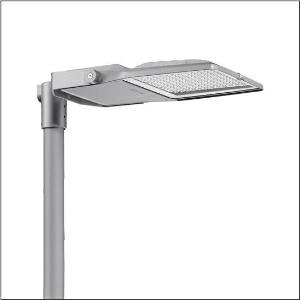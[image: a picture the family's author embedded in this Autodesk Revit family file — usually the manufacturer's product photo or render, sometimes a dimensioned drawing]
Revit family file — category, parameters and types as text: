
# Revit family: floodlight_fl_21_iq_midi___pl61_5xa7781e4c3a_96c8
name_source: partatom
category: Lighting Fixtures
units: mm (PartAtom-declared; Revit-internal decimal feet)

## family parameters
Cut with Voids When Loaded = No
Host = Face
Light Source = No
Part Type = Normal
Room Calculation Point = No
Round Connector Dimension = Use Diameter
Shared = No

## types (1)
- --- (1 x LED, 27490 lm, 208.1 W, 4000K)
    Apparent Load = 208 VA
    CIE Flux Codes = 33 65 98 100 100
    Color Rendering = 70
    Color Temperature = 4000K
    Default Elevation = 1800 mm
    Description = Floodlight FL 21 iQ midi, floodlight, primary light control with lens, of PMMA, primary optical cover: protective disc, of toughened safety glass, transparent, light distribution: PL61, light emission: direct distribution, installation type: surface-mounted, LED, High Power LED, rated luminous flux: 27.490lm, luminous efficacy: 132lm/W, light colour: 740, colour temperature: 4000K, control gear: ECG iQ, control: optimised constant luminous flux control (CLO 2.0), Desk-Remote (wireless, voltage-free reading and setting of iQ features in the workshop via application-optimized NFC function/RFID function), Light-Fading, Smart-Wire, Night-Set, Lumen-Switch, Temp-Guard, Auto-Match, with terminal, 6-pole, mains connection: 220..240V, AC, 50/60Hz, start of lifetime: 208W, end of service life: 227W, reduction: 90W, luminaire housing, of diecast aluminium, powder-coated, Siteco® metallic grey (DB 702S), corrosivity category C5 mid according to DIN EN ISO 12944, sealing non-destructively replaceable, please order mast flange separately, mast bracket, of steel, galvanised, powder-coated, Siteco® metallic grey (DB 702S), protection rating (complete): IP66, insulation class (complete): insulation class II (safety insulation), certification: CE, protection symbol: D, impact resistance: IK08, permissible operating ambient temperature: -40..+40°C, permissible operating ambient temperature for outdoor applications: -40..+50°C, standard: DIN EN 12944, LABS conformity tested according to VDMA 24364:2018-05, packaging unit: 1 piece

Light Distribution: PL61
    Height = 76 mm
    Lamp = 1 x LED
    Lamp Light Flux = 27490 lm
    Lamp Power = 208.1 W
    Lamp count = 1
    Length = 657 mm
    Luminous efficacy = 132 lm/W
    Manufacturer = Siteco
    ModVariant = No
    Model = 5XA7781E4C3A
    Number of Poles = 1
    OnlyDefault = Yes
    Power Factor = 1
    Product Name = Floodlight FL 21 iQ midi | PL61
    Product group = floodlight | pylon annexe
    ProductGroupID = 6200
    Protection Class = Protection class II
    Protection Degree = IP 66
    RLX_Detail_Level = 1
    RLX_Emergency_Light_Flux = 0 lm
    RLX_Emergency_Type = 0
    RLX_Emergency_Type_DB = No
    RlxData = <blob elided: 153693 chars, md5=2562d785>
    Socket = socket
    Standby Power = 0 W
    System Light Flux = 27490 lm
    System Power = 208 W
    Type Comments = factory setting: luminous flux: 100 % | dim-lin: 254 | 710 mA
    Type Image = l_1007123.jpg
    URL = http://relux.com
    VarID = @adj_057147
    Voltage = 0 V
    Weight = 0.00 kg
    Width = 442 mm

## geometry (parser evidence)
native form markers: Blend x4, Sweep x14
no freeform markers — native parametric forms only
